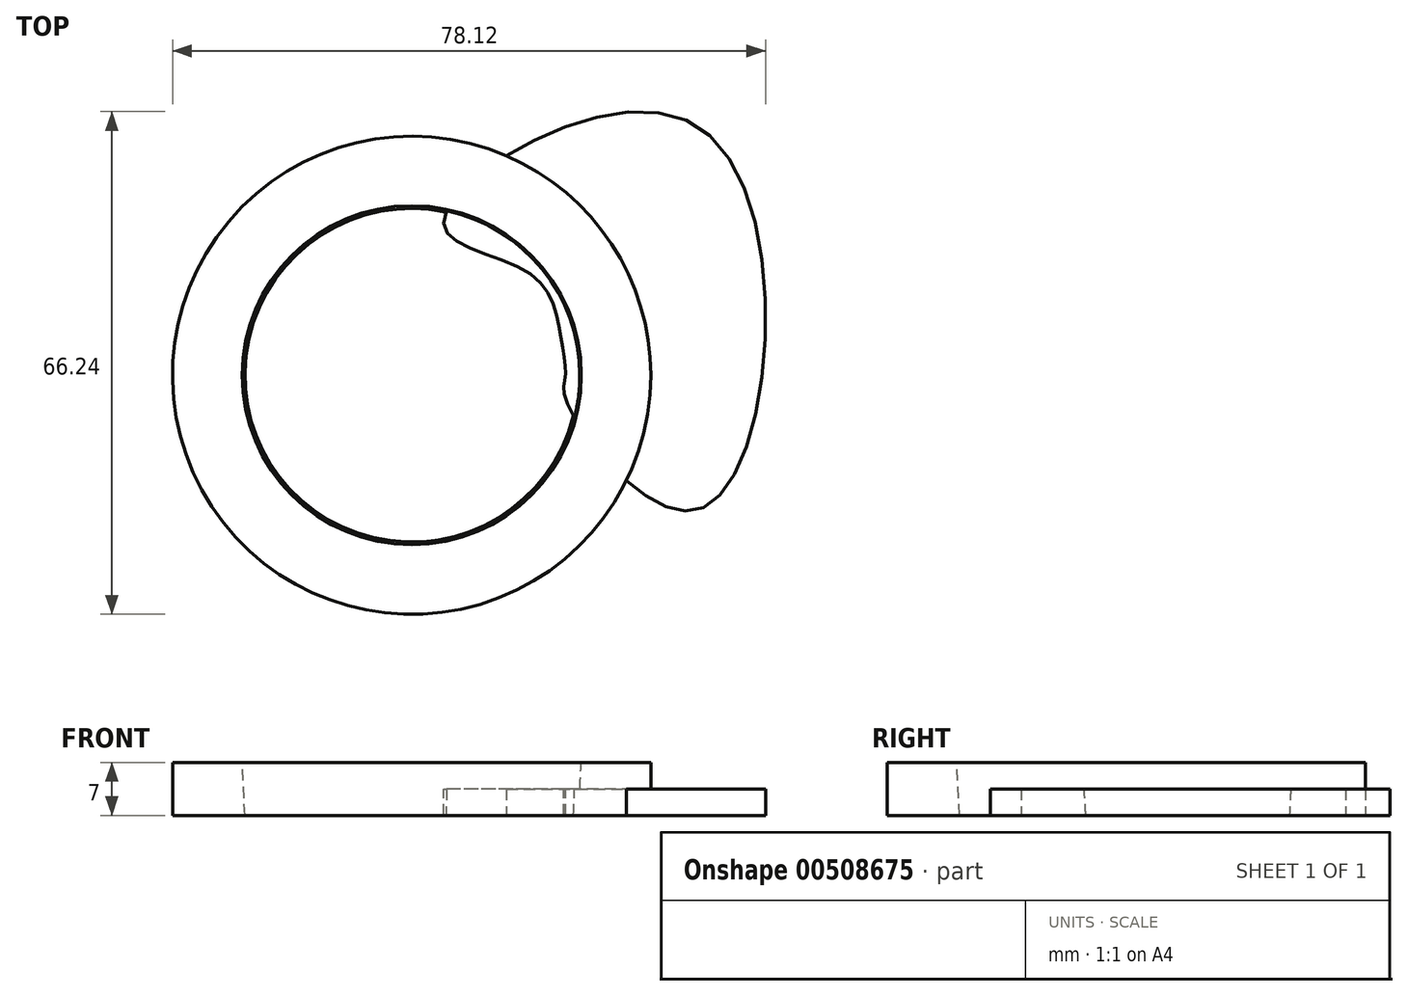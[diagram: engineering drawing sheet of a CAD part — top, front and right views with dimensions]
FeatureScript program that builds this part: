
annotation { "Feature Type Name" : "Feature", "Feature Type Description" : "" }
export const myFeature = defineFeature(function(context is Context, id is Id, definition is map)
    precondition{}
    {
        {
            var Q0;
            Q0=qCreatedBy(makeId("Top.planeOp"),FACE);
            var sketch = newSketch(context, id + "F0", { "sketchPlane" : qUnion([Q0])});
            skCircle(sketch, "E0", {"center": v(0, 0) * mm, "radius": 31.5 * mm});
            skCircle(sketch, "E1", {"center": v(0, 0) * mm, "radius": 21.97 * mm});
            skSolve(sketch);
        }
        {
            var Q0;
            Q0=makeQuery(id+"F0.imprint","IMPRINT",FACE,{"disambiguationData":[TD([[makeQuery(id+"F0.imprint","IMPRINT",EDGE,{"derivedFrom":sQuery(id+"F0.wireOp",EDGE,"E0")}),1.0]])]});
            extrude(context, id + "F1", {"entities" : qUnion([Q0]), "depth" : 7 * mm});
        }
        {
            var Q0;
            Q0=makeQuery(id+"F0.imprint","IMPRINT",FACE,{"disambiguationData":[TD([[makeQuery(id+"F0.imprint","IMPRINT",EDGE,{"derivedFrom":sQuery(id+"F0.wireOp",EDGE,"E1")}),1.0]])]});
            extrude(context, id + "F2", {"entities" : qUnion([Q0]), "operationType" : NewBodyOperationType.ADD, "depth" : 7 * mm});
        }
        {
            var Q0;
            Q0=makeQuery(id+"F0.imprint","IMPRINT",FACE,{"disambiguationData":[TD([[makeQuery(id+"F0.imprint","IMPRINT",EDGE,{"derivedFrom":sQuery(id+"F0.wireOp",EDGE,"E1")}),1.0]])]});
            extrude(context, id + "F3", {"entities" : qUnion([Q0]), "operationType" : NewBodyOperationType.REMOVE, "depth" : 25 * mm, "hasDraft" : true, "draftAngle" : 3 * degree});
        }
        {
            var Q0;
            Q0=qCreatedBy(makeId("Top.planeOp"),FACE);
            var sketch = newSketch(context, id + "F4", { "sketchPlane" : qUnion([Q0])});
            skFitSpline(sketch, "E2", {"points": [v(4.2, 20.3) * mm, v(37.8, 32.74) * mm, v(38.48, -17.42) * mm, v(20.52, -3.74) * mm, v(20.24, 0) * mm, v(19.55, 5.52) * mm, v(15.4, 13.53) * mm, v(4.2, 20.3) * mm]});
            skSolve(sketch);
        }
        {
            var Q0;
            Q0 = qSketchRegion(id + "F4", true);
            extrude(context, id + "F5", {"entities" : qUnion([Q0]), "operationType" : NewBodyOperationType.ADD, "depth" : (7 / 2) * mm});
        }
    });
